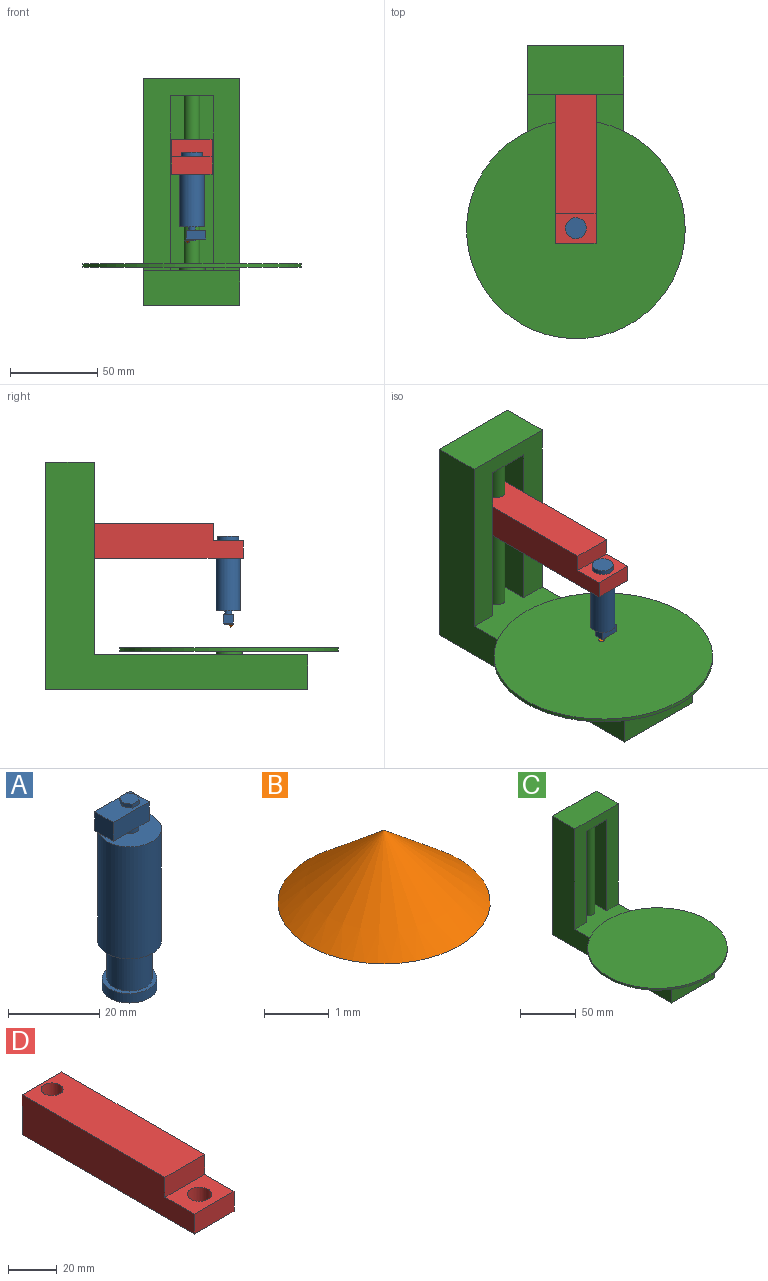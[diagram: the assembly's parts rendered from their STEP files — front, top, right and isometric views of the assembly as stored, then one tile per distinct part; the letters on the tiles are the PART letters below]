
ASSEMBLY  parts=4 mates=3
PART A: 21 faces, bbox 14.9x14x50.5 mm
  f0: plane 11.12x5.8mm, normal (0,0,1), area 51.6mm2, adj f9,f10,f11,f12,f14,f15,f16,f17
  f1: cylinder r=6mm len=12mm, axis (0,0,-1), area 94.2mm2, adj f2,f3
  f2: plane 12x12mm, normal (0,0,1), area 34.6mm2, adj f1,f4
  f3: plane 12x12mm, normal (0,0,-1), area 113.1mm2, adj f1
  f4: cylinder r=5mm len=10mm, axis (0,0,-1), area 314.2mm2, adj f2,f7
  f5: cylinder r=7mm len=30mm, axis (0,0,-1), area 1319.5mm2, adj f6,f7
  f6: plane 14x14mm, normal (0,0,1), area 141.4mm2, adj f5,f8
  f7: plane 14x14mm, normal (0,0,-1), area 75.4mm2, adj f4,f5
  f8: cylinder r=2mm len=4mm, axis (0,0,-1), area 25.1mm2, adj f6,f13
  f9: plane 5.8x5mm, normal (-1,0,0), area 29mm2, adj f0,f10,f12,f13
  f10: plane 11.12x5mm, normal (0,-1,0), area 55.6mm2, adj f0,f9,f11,f13
  f11: plane 5.8x5mm, normal (1,0,0), area 29mm2, adj f0,f10,f12,f13
  f12: plane 11.12x5mm, normal (0,1,0), area 55.6mm2, adj f0,f9,f11,f13
  f13: plane 11.12x5.8mm, normal (0,0,-1), area 51.8mm2, adj f8,f9,f10,f11,f12
  f14: plane 2.22x1mm, normal (0,1,0), area 2.2mm2, adj f0,f15,f19,f20
  f15: plane 1.92x1.11mm, normal (-0.87,0.5,0), area 2.2mm2, adj f0,f14,f16,f20
  f16: plane 1.92x1.11mm, normal (-0.87,-0.5,0), area 2.2mm2, adj f0,f15,f17,f20
  f17: plane 2.22x1mm, normal (0,-1,0), area 2.2mm2, adj f0,f16,f18,f20
  f18: plane 1.92x1.11mm, normal (0.87,-0.5,0), area 2.2mm2, adj f0,f17,f19,f20
  f19: plane 1.92x1.11mm, normal (0.87,0.5,0), area 2.2mm2, adj f0,f14,f18,f20
  f20: plane 4.44x3.85mm, normal (0,0,1), area 12.8mm2, adj f14,f15,f16,f17,f18,f19
PART B: 2 faces, bbox 3.3x3.3x1.4 mm
  f0: plane 3.28x3.28mm, normal (0,0,-1), area 8.5mm2, adj f1
  f1: cone r=0mm half-angle=50.2deg, axis (0,0,-1), area 11mm2, adj f0
PART C: 17 faces, bbox 125x167.5x130 mm
  f0: plane 140x55mm, normal (0,0,1), area 6919.7mm2, adj f1,f2,f4,f6,f7,f8,f9,f10
  f1: plane 55x20mm, normal (0,-1,0), area 1100mm2, adj f0,f2,f4,f5
  f2: plane 150x130mm, normal (1,0,0), area 6080mm2, adj f0,f1,f3,f5,f6,f15
  f3: plane 130x55mm, normal (0,1,0), area 7150mm2, adj f2,f4,f5,f15
  f4: plane 150x130mm, normal (-1,0,0), area 6080mm2, adj f0,f1,f3,f5,f6,f15
  f5: plane 150x55mm, normal (0,0,-1), area 8250mm2, adj f1,f2,f3,f4
  f6: plane 110x55mm, normal (0,-1,0), area 3550mm2, adj f0,f2,f4,f7,f9,f15,f16
  f7: plane 100x18mm, normal (1,0,0), area 1800mm2, adj f0,f6,f8,f16
  f8: plane 100x25mm, normal (0,-1,0), area 2500mm2, adj f0,f7,f9,f16
  f9: plane 100x18mm, normal (-1,0,0), area 1800mm2, adj f0,f6,f8,f16
  f10: cylinder r=4.5mm len=100mm, axis (0,0,-1), area 2827.4mm2, adj f0,f16
  f11: cylinder r=7.5mm len=15mm, axis (0,0,-1), area 94.2mm2, adj f0,f14
  f12: cylinder r=62.5mm len=125mm, axis (0,0,-1), area 785.4mm2, adj f13,f14
  f13: plane 125x125mm, normal (0,0,1), area 12271.8mm2, adj f12
  f14: plane 125x125mm, normal (0,0,-1), area 12095.1mm2, adj f11,f12
  f15: plane 55x28mm, normal (0,0,1), area 1540mm2, adj f2,f3,f4,f6
  f16: plane 25x18mm, normal (0,0,-1), area 386.4mm2, adj f6,f7,f8,f9,f10
PART D: 10 faces, bbox 23x100x20 mm
  f0: plane 23x20mm, normal (0,1,0), area 460mm2, adj f1,f3,f4,f5
  f1: plane 100x20mm, normal (-1,0,0), area 1829.3mm2, adj f0,f2,f4,f5,f6,f7
  f2: plane 23x10mm, normal (0,-1,0), area 230mm2, adj f1,f3,f4,f7
  f3: plane 100x20mm, normal (1,0,0), area 1829.3mm2, adj f0,f2,f4,f5,f6,f7
  f4: plane 82.93x23mm, normal (0,0,1), area 1843.8mm2, adj f0,f1,f2,f3,f9
  f5: plane 100x23mm, normal (0,0,-1), area 2157.8mm2, adj f0,f1,f3,f6,f8,f9
  f6: plane 23x10mm, normal (0,-1,0), area 230mm2, adj f1,f3,f5,f7
  f7: plane 23x17.07mm, normal (0,0,1), area 314.1mm2, adj f1,f2,f3,f6,f8
  f8: cylinder r=5mm len=10mm, axis (0,0,1), area 314.2mm2, adj f5,f7
  f9: cylinder r=4.5mm len=20mm, axis (0,0,1), area 565.5mm2, adj f4,f5
PLACE A rot(axis=(0,1,0),180deg) t=(-2.69,30.99,62.39)mm
PLACE B rot(axis=(-1,0,0),180deg) t=(-5.12,29.44,62.41)mm
PLACE C t=(-2.69,60.46,-25.2)mm
PLACE D rot(axis=(0,1,0),0deg) t=(-2.69,72.46,49.92)mm
MATE cylindrical D.f9 <-> C.f10  axis (0,0,1) through (-2.69,116.46,69.92)mm
MATE cylindrical A.f4 <-> D.f8  axis (0,0,1) through (-2.69,30.99,54.89)mm
MATE planar B.f1 <-> A.f8  axis (0,0,1) through (-5.12,29.44,11.89)mm
